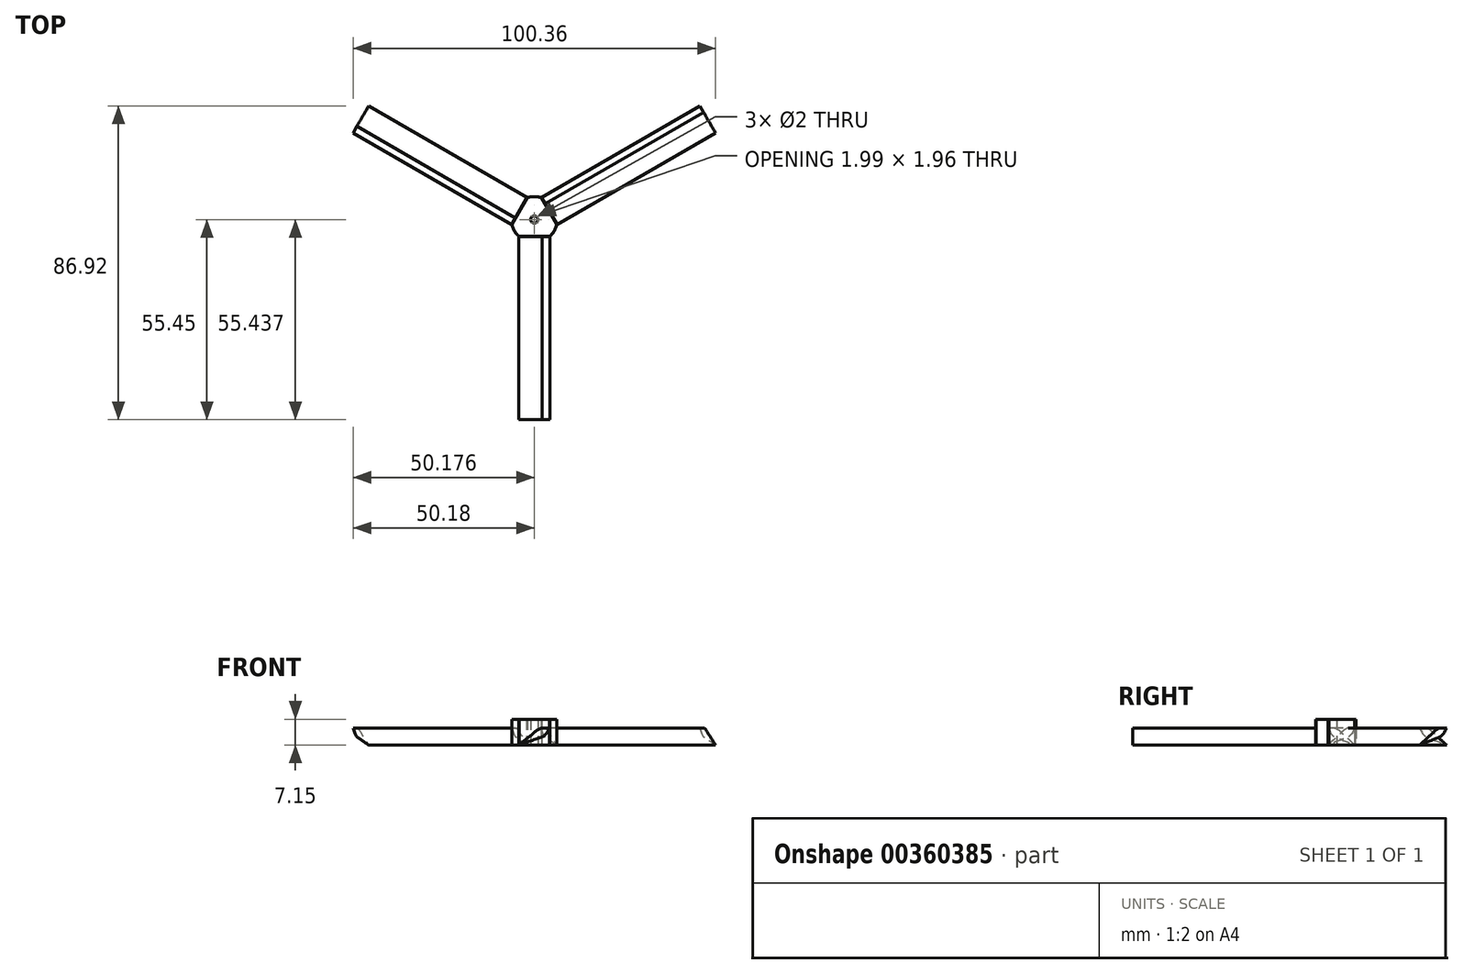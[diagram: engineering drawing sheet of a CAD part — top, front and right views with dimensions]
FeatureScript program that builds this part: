
annotation { "Feature Type Name" : "Feature", "Feature Type Description" : "" }
export const myFeature = defineFeature(function(context is Context, id is Id, definition is map)
    precondition{}
    {
        {
            var Q0;
            Q0=qCreatedBy(makeId("Top.planeOp"),FACE);
            var sketch = newSketch(context, id + "F0", { "sketchPlane" : qUnion([Q0])});
            skCircle(sketch, "E0", {"center": v(0, 0) * mm, "radius": 1 * mm});
            skCircle(sketch, "E1", {"center": v(0, 0) * mm, "radius": 6.35 * mm});
            skSolve(sketch);
        }
        {
            var Q0;
            Q0 = qSketchRegion(id + "F0", true);
            extrude(context, id + "F1", {"entities" : qUnion([Q0]), "depth" : 9.52 * mm});
        }
        {
            var Q0;
            Q0=makeQuery(id+"F1.opExtrude","CAP_FACE",FACE,{"disambiguationData":[OSD([sQuery(id+"F0.wireOp",EDGE,"E0"),sQuery(id+"F0.wireOp",EDGE,"E1")])],"isStart":false});
            cPlane(context, id + "F2", {"entities" : qUnion([Q0]), "cplaneType" : CPlaneType.OFFSET, "offset" : 0 * mm, "width" : 152.4 * mm, "height" : 152.4 * mm});
        }
        {
            var Q0;
            Q0=qCreatedBy(id+"F2.planeOp",FACE);
            var sketch = newSketch(context, id + "F3", { "sketchPlane" : qUnion([Q0])});
            skLineSegment(sketch, "E2.0", {"start": v(8.24, -4.65) * mm, "end": v(0, 9.62) * mm});
            skLineSegment(sketch, "E3.0", {"start": v(0, 9.62) * mm, "end": v(-8.24, -4.65) * mm});
            skLineSegment(sketch, "E4.0", {"start": v(-8.24, -4.65) * mm, "end": v(8.24, -4.65) * mm});
            skLineSegment(sketch, "E5.0", {"start": v(19.24, -11) * mm, "end": v(0, 22.32) * mm});
            skLineSegment(sketch, "E6.0", {"start": v(-19.24, -11) * mm, "end": v(19.24, -11) * mm});
            skLineSegment(sketch, "E7.0", {"start": v(0, 9.62) * mm, "end": v(-8.24, -4.66) * mm});
            skLineSegment(sketch, "E8.0", {"start": v(0, 22.32) * mm, "end": v(-19.24, -11) * mm});
            skPoint(sketch, "E9.start.orphan", {"position": v(0, 6.45) * mm});
            skSolve(sketch);
        }
        {
            var Q0;
            {var subQ1=sQuery(id+"F3.wireOp",EDGE,"E3.0");Q0=makeQuery(id+"F3.imprint","IMPRINT",FACE,{"disambiguationData":[TD([[makeQuery(id+"F3.imprint","IMPRINT",EDGE,{"derivedFrom":subQ1}),-1.0]])]});}
            extrude(context, id + "F4", {"entities" : qUnion([Q0]), "operationType" : NewBodyOperationType.REMOVE, "oppositeDirection" : true, "depth" : 25.4 * mm});
        }
        {
            var Q0;
            Q0=makeQuery(id+"F4.boolean.opBoolean","COPY",FACE,{"derivedFrom":makeQuery(id+"F4.opExtrude","SWEPT_FACE",FACE,{"disambiguationData":[OSD([sQuery(id+"F3.wireOp",EDGE,"E4.0")])]})});
            var sketch = newSketch(context, id + "F5", { "sketchPlane" : qUnion([Q0])});
            skLineSegment(sketch, "E10", {"start": v(4.32, 9.53) * mm, "end": v(4.32, 0) * mm});
            skLineSegment(sketch, "E11", {"start": v(-4.32, 9.53) * mm, "end": v(4.32, 9.53) * mm});
            skLineSegment(sketch, "E12", {"start": v(-4.32, 0) * mm, "end": v(4.32, 0) * mm});
            skLineSegment(sketch, "E13.0", {"start": v(-4.32, 7.14) * mm, "end": v(4.32, 7.14) * mm});
            skLineSegment(sketch, "E14.0", {"start": v(-4.32, 2.38) * mm, "end": v(4.32, 2.38) * mm});
            skFitSpline(sketch, "E15", {"points": [v(4.32, 7.14) * mm, v(2.9, 5.06) * mm, v(1.37, 4.32) * mm, v(-1.18, 3.49) * mm, v(-4.32, 2.38) * mm], "startDerivative": vector(-5.32, -9.66) * mm, "endDerivative": vector(-11.05, -3.97) * mm});
            skFitSpline(sketch, "E16.MirrorCS", {"points": [v(4.32, 7.14) * mm, v(1.8, 7.05) * mm, v(0.36, 6.16) * mm, v(-1.71, 4.44) * mm, v(-4.32, 2.38) * mm], "startDerivative": vector(-11, 0.66) * mm, "endDerivative": vector(-9.25, -7.23) * mm});
            skSolve(sketch);
        }
        {
            var Q0;
            {var subQ1=sQuery(id+"F5.wireOp",EDGE,"E15");Q0=makeQuery(id+"F5.imprint","IMPRINT",FACE,{"disambiguationData":[TD([[makeQuery(id+"F5.imprint","IMPRINT",EDGE,{"derivedFrom":subQ1}),-1.0]])]});}
            extrude(context, id + "F6", {"entities" : qUnion([Q0]), "operationType" : NewBodyOperationType.ADD, "depth" : 50.8 * mm});
        }
        {
            var Q0;
            Q0=makeQuery(id+"F1.opExtrude","SWEPT_BODY",BODY,{"disambiguationData":[OSD([sQuery(id+"F0.wireOp",EDGE,"E0"),sQuery(id+"F0.wireOp",EDGE,"E1")])]});
            var Q1;
            Q1=makeQuery(id+"F1.opExtrude","CAP_EDGE",EDGE,{"disambiguationData":[OSD([sQuery(id+"F0.wireOp",EDGE,"E0")])],"isStart":false});
            circularPattern(context, id + "F7", {"entities" : qUnion([Q0]), "axis" : qUnion([Q1]), "angle" : 360 * degree, "instanceCount" : 3, "equalSpace" : true});
        }
        {
            var Q0;
            Q0=makeQuery(id+"F7.opPattern","COPY",FACE,{"derivedFrom":makeQuery(id+"F4.boolean.opBoolean","COPY",FACE,{"derivedFrom":makeQuery(id+"F4.opExtrude","SWEPT_FACE",FACE,{"disambiguationData":[OSD([sQuery(id+"F3.wireOp",EDGE,"E3.0")])]})}),"instanceName":"1"});
            var sketch = newSketch(context, id + "F8", { "sketchPlane" : qUnion([Q0])});
            skLineSegment(sketch, "E17.bottom", {"start": v(-6.24, 2.38) * mm, "end": v(6.53, 2.38) * mm});
            skLineSegment(sketch, "E17.top", {"start": v(-6.24, -0.22) * mm, "end": v(6.53, -0.22) * mm});
            skLineSegment(sketch, "E17.left", {"start": v(-6.24, 2.38) * mm, "end": v(-6.24, -0.22) * mm});
            skLineSegment(sketch, "E17.right", {"start": v(6.53, 2.38) * mm, "end": v(6.53, -0.22) * mm});
            skSolve(sketch);
        }
        {
            var Q0;
            {var subQ1=makeQuery(id+"F4.opExtrude","SWEPT_FACE",FACE,{"disambiguationData":[OSD([sQuery(id+"F3.wireOp",EDGE,"E3.0")])]});var subQ2=sQuery(id+"F0.wireOp",EDGE,"E1");var subQ8=makeQuery(id+"F7.opPattern","COPY",EDGE,{"derivedFrom":makeQuery(id+"F4.boolean.opBoolean","INTERSECT",EDGE,{"derivedFrom":[makeQuery(id+"F1.opExtrude","CAP_FACE",FACE,{"disambiguationData":[OSD([sQuery(id+"F0.wireOp",EDGE,"E0"),subQ2])],"isStart":true}),subQ1]}),"instanceName":"1"});Q0=makeQuery(id+"F8.imprint","IMPRINT",FACE,{"disambiguationData":[TD([[makeQuery(id+"F8.imprint","IMPRINT",EDGE,{"derivedFrom":subQ8}),1.0]])]});}
            var Q1;
            Q1=makeQuery(id+"F8.imprint","IMPRINT",FACE,{"disambiguationData":[TD([[makeQuery(id+"F8.imprint","IMPRINT",EDGE,{"derivedFrom":sQuery(id+"F8.wireOp",EDGE,"E17.top")}),1.0]])]});
            extrude(context, id + "F9", {"entities" : qUnion([Q0, Q1]), "operationType" : NewBodyOperationType.REMOVE, "oppositeDirection" : true, "depth" : 25.4 * mm});
        }
    });
